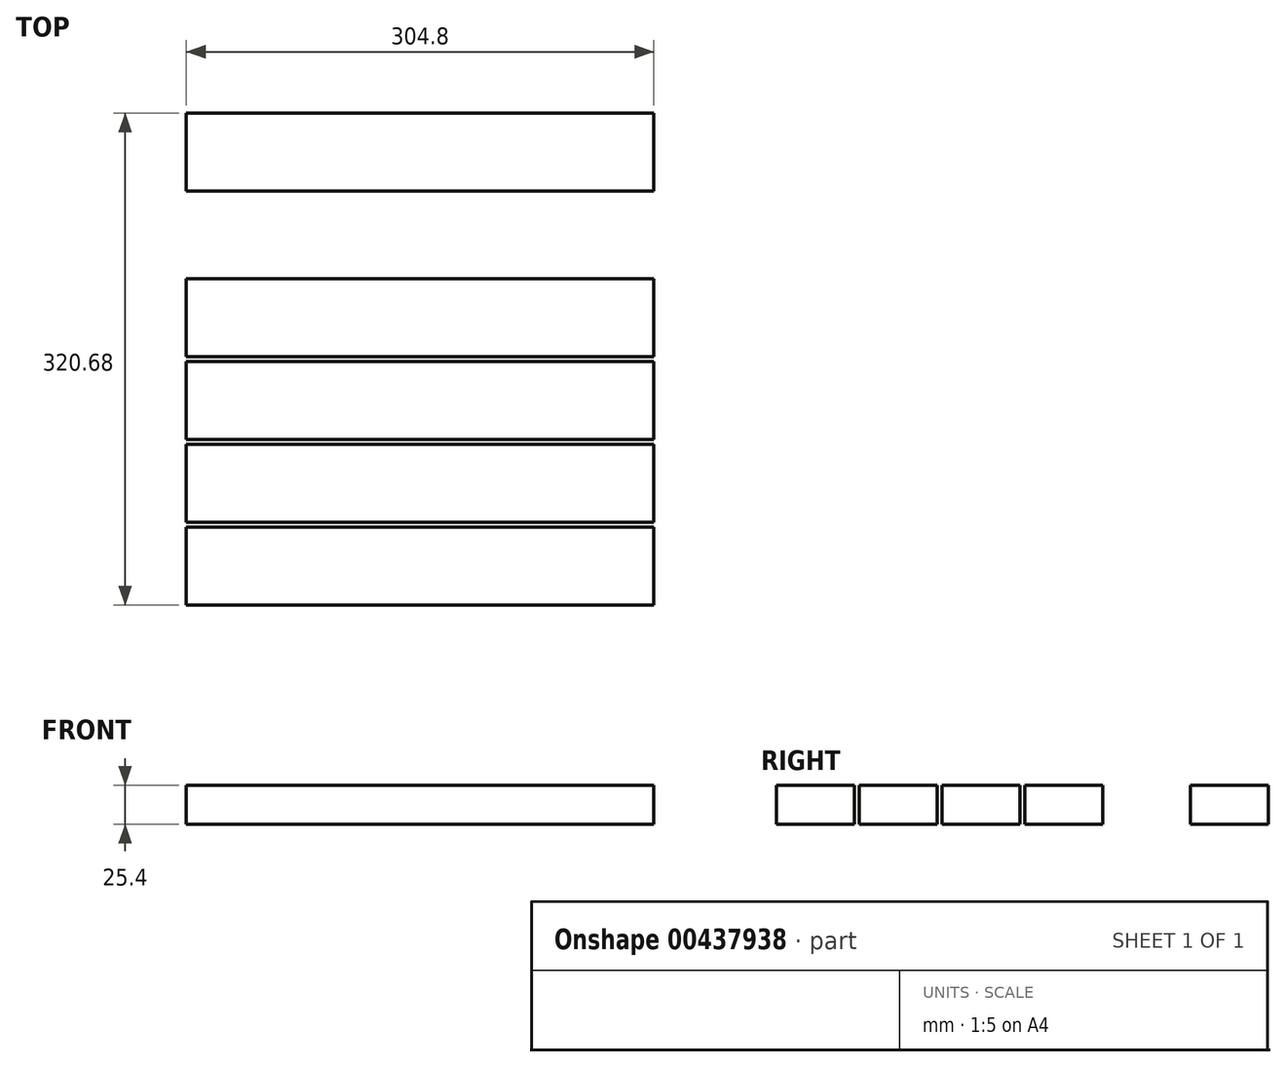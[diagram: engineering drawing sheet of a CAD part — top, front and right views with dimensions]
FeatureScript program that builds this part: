
annotation { "Feature Type Name" : "Feature", "Feature Type Description" : "" }
export const myFeature = defineFeature(function(context is Context, id is Id, definition is map)
    precondition{}
    {
        {
            var Q0;
            Q0=qCreatedBy(makeId("Top.planeOp"),FACE);
            var Q1;
            Q1=qCreatedBy(makeId("Top.planeOp"),FACE);
            var sketch = newSketch(context, id + "F0", { "sketchPlane" : qUnion([Q0, Q1])});
            skLineSegment(sketch, "E0.bottom", {"start": v(0, 0) * mm, "end": v(304.8, 0) * mm});
            skLineSegment(sketch, "E0.top", {"start": v(0, 50.8) * mm, "end": v(304.8, 50.8) * mm});
            skLineSegment(sketch, "E0.left", {"start": v(0, 0) * mm, "end": v(0, 50.8) * mm});
            skLineSegment(sketch, "E0.right", {"start": v(304.8, 0) * mm, "end": v(304.8, 50.8) * mm});
            skLineSegment(sketch, "E1.0.1.0", {"start": v(0, -53.98) * mm, "end": v(0, -3.17) * mm});
            skLineSegment(sketch, "E1.0.1.1", {"start": v(304.8, -53.97) * mm, "end": v(304.8, -3.17) * mm});
            skLineSegment(sketch, "E1.0.1.2", {"start": v(0, -3.17) * mm, "end": v(304.8, -3.17) * mm});
            skLineSegment(sketch, "E1.0.1.3", {"start": v(0, -53.98) * mm, "end": v(304.8, -53.98) * mm});
            skLineSegment(sketch, "E1.0.2.0", {"start": v(0, -107.95) * mm, "end": v(0, -57.15) * mm});
            skLineSegment(sketch, "E1.0.2.1", {"start": v(304.8, -107.95) * mm, "end": v(304.8, -57.15) * mm});
            skLineSegment(sketch, "E1.0.2.2", {"start": v(0, -57.15) * mm, "end": v(304.8, -57.15) * mm});
            skLineSegment(sketch, "E1.0.2.3", {"start": v(0, -107.95) * mm, "end": v(304.8, -107.95) * mm});
            skLineSegment(sketch, "E1.0.3.0", {"start": v(0, -161.93) * mm, "end": v(0, -111.12) * mm});
            skLineSegment(sketch, "E1.0.3.1", {"start": v(304.8, -161.93) * mm, "end": v(304.8, -111.12) * mm});
            skLineSegment(sketch, "E1.0.3.2", {"start": v(0, -111.12) * mm, "end": v(304.8, -111.12) * mm});
            skLineSegment(sketch, "E1.0.3.3", {"start": v(0, -161.93) * mm, "end": v(304.8, -161.93) * mm});
            skLineSegment(sketch, "E1.0.4.0", {"start": v(0, -215.9) * mm, "end": v(0, -165.1) * mm});
            skLineSegment(sketch, "E1.0.4.1", {"start": v(304.8, -215.9) * mm, "end": v(304.8, -165.1) * mm});
            skLineSegment(sketch, "E1.0.4.2", {"start": v(0, -165.1) * mm, "end": v(304.8, -165.1) * mm});
            skLineSegment(sketch, "E1.0.4.3", {"start": v(0, -215.9) * mm, "end": v(304.8, -215.9) * mm});
            skLineSegment(sketch, "E1.0.5.0", {"start": v(0, -269.88) * mm, "end": v(0, -219.08) * mm});
            skLineSegment(sketch, "E1.0.5.1", {"start": v(304.8, -269.88) * mm, "end": v(304.8, -219.08) * mm});
            skLineSegment(sketch, "E1.0.5.2", {"start": v(0, -219.08) * mm, "end": v(304.8, -219.08) * mm});
            skLineSegment(sketch, "E1.0.5.3", {"start": v(0, -269.88) * mm, "end": v(304.8, -269.88) * mm});
            skLineSegment(sketch, "E1.direction1", {"start": v(0, 0) * mm, "end": v(25.4, 0) * mm, "construction": true});
            skLineSegment(sketch, "E1.direction2", {"start": v(0, 0) * mm, "end": v(0, -53.98) * mm, "construction": true});
            skSolve(sketch);
        }
        {
            var Q0;
            Q0 = qSketchRegion(id + "F0", true);
            extrude(context, id + "F1", {"entities" : qUnion([Q0]), "depth" : 25.4 * mm});
        }
        {
            var Q0;
            Q0=makeQuery(id+"F1.opExtrude","CAP_FACE",FACE,{"disambiguationData":[OSD([sQuery(id+"F0.wireOp",EDGE,"E0.bottom"),sQuery(id+"F0.wireOp",EDGE,"E0.top"),sQuery(id+"F0.wireOp",EDGE,"E0.left"),sQuery(id+"F0.wireOp",EDGE,"E0.right")])],"isStart":false});
            var sketch = newSketch(context, id + "F2", { "sketchPlane" : qUnion([Q0])});
            skSolve(sketch);
        }
        {
            var Q0;
            Q0 = qSketchRegion(id + "F2", true);
            var Q1;
            Q1=makeQuery(id+"F2.imprint","IMPRINT",FACE,{"disambiguationData":[TD([[makeQuery(id+"F2.imprint","IMPRINT",EDGE,{"derivedFrom":makeQuery(id+"F1.opExtrude","CAP_EDGE",EDGE,{"disambiguationData":[OSD([sQuery(id+"F0.wireOp",EDGE,"E0.bottom")])],"isStart":false})}),1.0]])]});
            var Q2;
            Q2=makeQuery(id+"F1.opExtrude","CAP_FACE",FACE,{"disambiguationData":[OSD([sQuery(id+"F0.wireOp",EDGE,"E1.0.1.0"),sQuery(id+"F0.wireOp",EDGE,"E1.0.1.1"),sQuery(id+"F0.wireOp",EDGE,"E1.0.1.2"),sQuery(id+"F0.wireOp",EDGE,"E1.0.1.3")])],"isStart":false});
            extrude(context, id + "F3", {"entities" : qUnion([Q0, Q1, Q2]), "operationType" : NewBodyOperationType.REMOVE, "oppositeDirection" : true, "depth" : 25.4 * mm});
        }
    });
